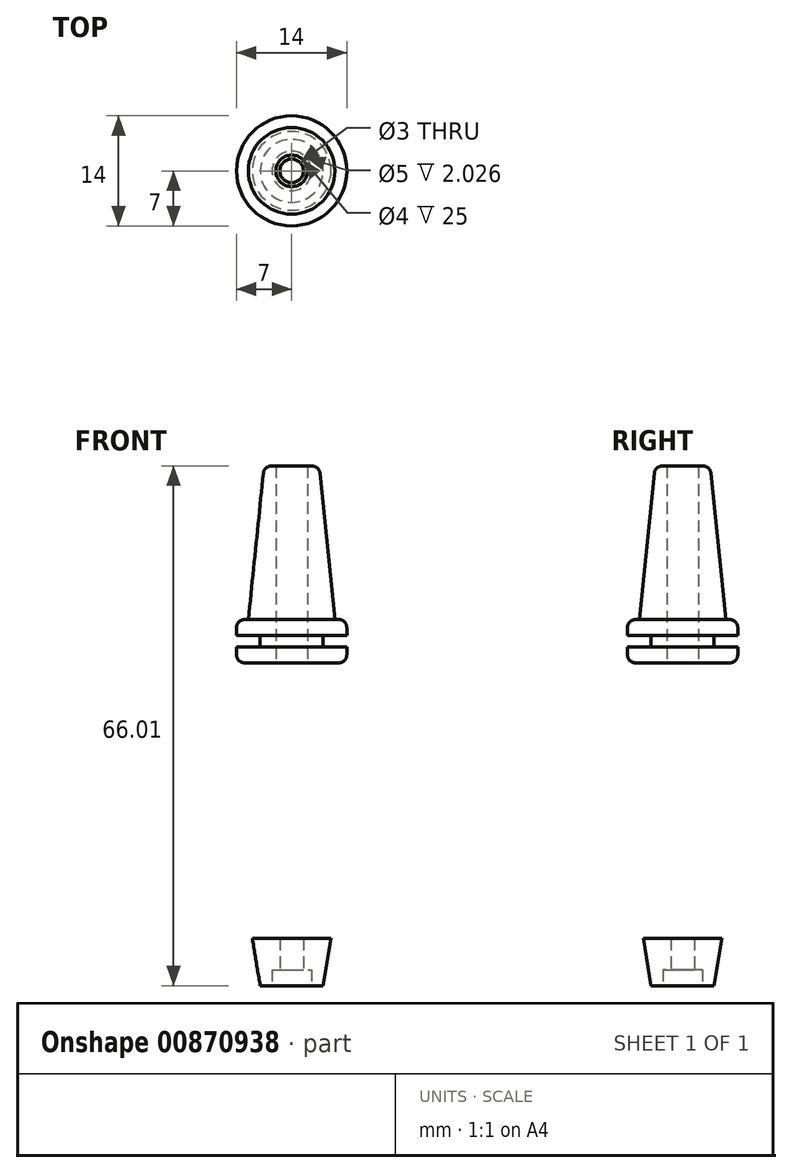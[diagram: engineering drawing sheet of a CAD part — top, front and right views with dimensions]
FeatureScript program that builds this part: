
annotation { "Feature Type Name" : "Feature", "Feature Type Description" : "" }
export const myFeature = defineFeature(function(context is Context, id is Id, definition is map)
    precondition{}
    {
        {
            var Q0;
            Q0=qCreatedBy(makeId("Front.planeOp"),FACE);
            var sketch = newSketch(context, id + "F0", { "sketchPlane" : qUnion([Q0])});
            skLineSegment(sketch, "E0", {"start": v(0, 33.52) * mm, "end": v(0, 79.96) * mm, "construction": true});
            skLineSegment(sketch, "E1", {"start": v(2, 70.67) * mm, "end": v(2, 45.67) * mm});
            skLineSegment(sketch, "E2", {"start": v(2, 45.67) * mm, "end": v(7, 45.67) * mm});
            skLineSegment(sketch, "E3", {"start": v(7, 45.67) * mm, "end": v(7, 47.67) * mm});
            skLineSegment(sketch, "E4", {"start": v(7, 47.67) * mm, "end": v(4, 47.67) * mm});
            skLineSegment(sketch, "E5", {"start": v(4, 47.67) * mm, "end": v(4, 49.17) * mm});
            skLineSegment(sketch, "E6", {"start": v(4, 49.17) * mm, "end": v(7, 49.17) * mm});
            skLineSegment(sketch, "E7", {"start": v(7, 49.17) * mm, "end": v(7, 51.17) * mm});
            skLineSegment(sketch, "E8", {"start": v(7, 51.17) * mm, "end": v(5.5, 51.17) * mm});
            skLineSegment(sketch, "E9", {"start": v(5.5, 51.17) * mm, "end": v(3.5, 70.67) * mm});
            skLineSegment(sketch, "E10", {"start": v(3.5, 70.67) * mm, "end": v(2, 70.67) * mm});
            skSolve(sketch);
        }
        {
            var Q0;
            Q0 = qSketchRegion(id + "F0", true);
            var Q1;
            Q1=sQuery(id+"F0.wireOp",EDGE,"E0");
            revolve(context, id + "F1", {"surfaceOperationType" : NewSurfaceOperationType.NEW, "entities" : qUnion([Q0]), "axis" : qUnion([Q1]), "revolveType" : RevolveType.FULL});
        }
        {
            var Q0;
            Q0=makeQuery(id+"F1.opRevolve","SWEPT_EDGE",EDGE,{"disambiguationData":[OSD([sQuery(id+"F0.wireOp",EDGE,"E7"),sQuery(id+"F0.wireOp",EDGE,"E8")])]});
            var Q1;
            Q1=makeQuery(id+"F1.opRevolve","SWEPT_EDGE",EDGE,{"disambiguationData":[OSD([sQuery(id+"F0.wireOp",EDGE,"E2"),sQuery(id+"F0.wireOp",EDGE,"E3")])]});
            var Q2;
            Q2=makeQuery(id+"F1.opRevolve","SWEPT_EDGE",EDGE,{"disambiguationData":[OSD([sQuery(id+"F0.wireOp",EDGE,"E9"),sQuery(id+"F0.wireOp",EDGE,"E10")])]});
            fillet(context, id + "F2", {"entities" : qUnion([Q0, Q1, Q2]), "radius" : 1 * mm, "tangentPropagation" : true, "allowEdgeOverflow" : false});
        }
        {
            var Q0;
            Q0=qCreatedBy(makeId("Front.planeOp"),FACE);
            var sketch = newSketch(context, id + "F3", { "sketchPlane" : qUnion([Q0])});
            skLineSegment(sketch, "E11", {"start": v(0, 5.77) * mm, "end": v(0, 15.01) * mm, "construction": true});
            skLineSegment(sketch, "E12", {"start": v(1.5, 10.66) * mm, "end": v(1.5, 6.69) * mm});
            skLineSegment(sketch, "E13", {"start": v(1.5, 6.69) * mm, "end": v(2.5, 6.69) * mm});
            skLineSegment(sketch, "E14", {"start": v(2.5, 6.69) * mm, "end": v(2.5, 4.66) * mm});
            skLineSegment(sketch, "E15", {"start": v(2.5, 4.66) * mm, "end": v(4, 4.66) * mm});
            skLineSegment(sketch, "E16", {"start": v(4, 4.66) * mm, "end": v(5, 10.66) * mm});
            skLineSegment(sketch, "E17", {"start": v(5, 10.66) * mm, "end": v(1.5, 10.66) * mm});
            skSolve(sketch);
        }
        {
            var Q0;
            Q0 = qSketchRegion(id + "F3", true);
            var Q1;
            Q1=sQuery(id+"F3.wireOp",EDGE,"E11");
            revolve(context, id + "F4", {"surfaceOperationType" : NewSurfaceOperationType.NEW, "entities" : qUnion([Q0]), "axis" : qUnion([Q1]), "revolveType" : RevolveType.FULL});
        }
    });
